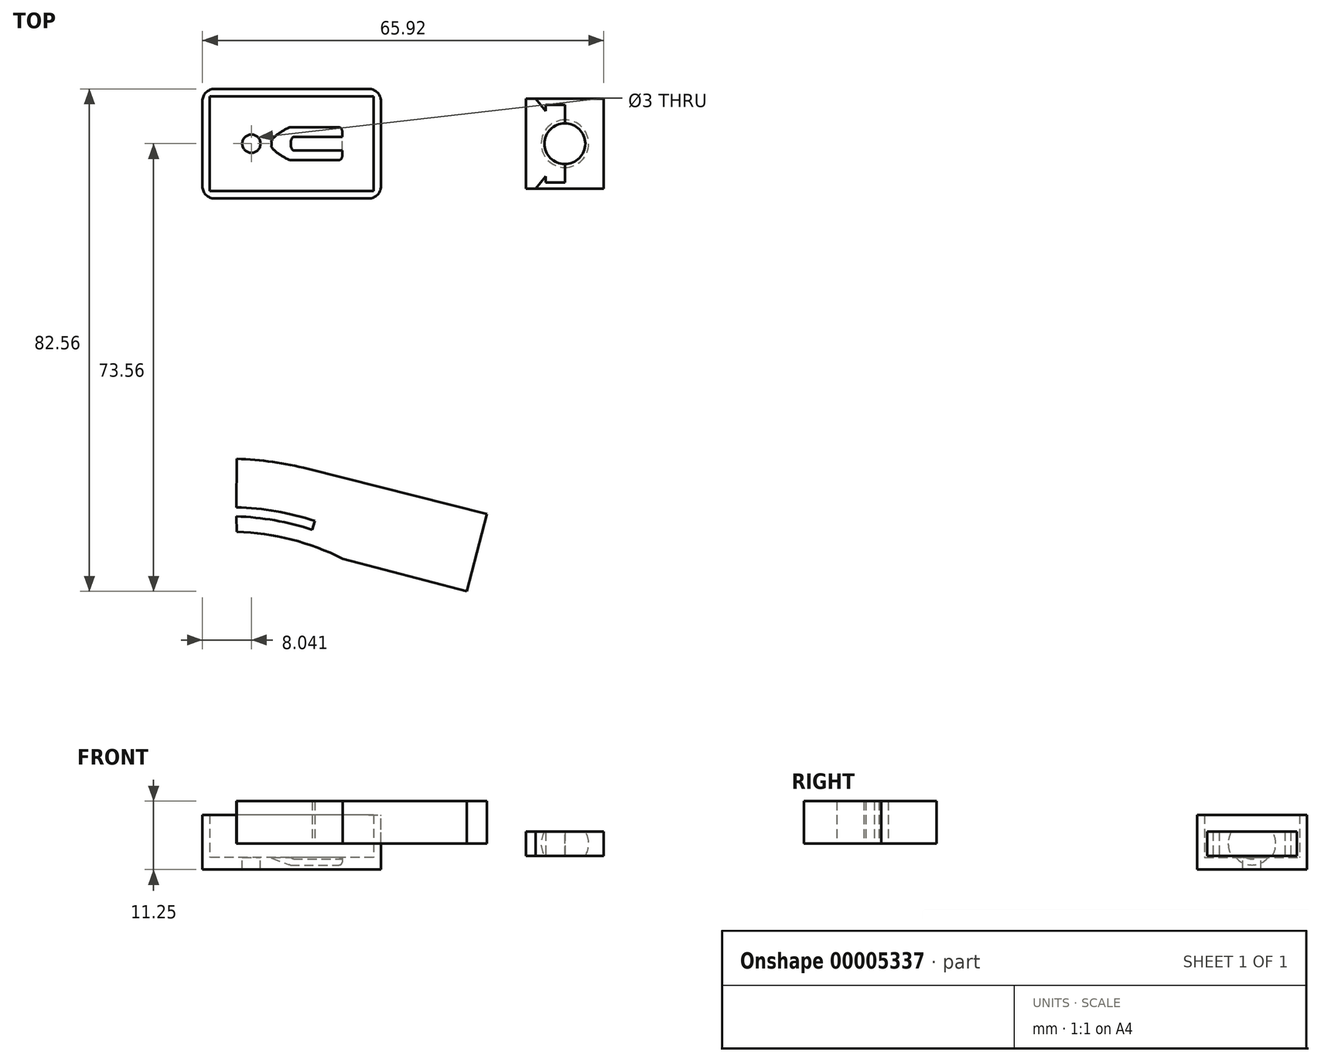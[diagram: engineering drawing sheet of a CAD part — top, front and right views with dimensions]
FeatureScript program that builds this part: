
annotation { "Feature Type Name" : "Feature", "Feature Type Description" : "" }
export const myFeature = defineFeature(function(context is Context, id is Id, definition is map)
    precondition{}
    {
        {
            var Q0;
            Q0=qCreatedBy(makeId("Top.planeOp"),FACE);
            var sketch = newSketch(context, id + "F0", { "sketchPlane" : qUnion([Q0])});
            skLineSegment(sketch, "E0", {"start": v(-22.32, 3.5) * mm, "end": v(-14.3, 3.5) * mm});
            skLineSegment(sketch, "E1", {"start": v(-13.8, 3) * mm, "end": v(-13.8, 2.5) * mm});
            skLineSegment(sketch, "E2", {"start": v(-13.8, 2.5) * mm, "end": v(-21.8, 2.5) * mm});
            skLineSegment(sketch, "E3", {"start": v(-22.3, 2) * mm, "end": v(-22.3, 0) * mm});
            skPoint(sketch, "E4.orphan", {"position": v(-13.8, 0) * mm});
            skLineSegment(sketch, "E5", {"start": v(-34.86, 0) * mm, "end": v(-13.8, 0) * mm});
            skPoint(sketch, "E6.visualSharp", {"position": v(-22.62, 3.5) * mm});
            skArc(sketch, "E6.filletArc", {"start": v(-22.32, 3.5) * mm, "mid": v(-22.51, 3.48) * mm, "end": v(-22.7, 3.43) * mm});
            skPoint(sketch, "E7.visualSharp", {"position": v(-22.3, 2.5) * mm});
            skArc(sketch, "E7.filletArc", {"start": v(-21.8, 2.5) * mm, "mid": v(-22.16, 2.35) * mm, "end": v(-22.3, 2) * mm});
            skPoint(sketch, "E8.visualSharp", {"position": v(-13.8, 3.5) * mm});
            skArc(sketch, "E8.filletArc", {"start": v(-13.8, 3) * mm, "mid": v(-13.95, 3.35) * mm, "end": v(-14.3, 3.5) * mm});
            skCircle(sketch, "E9", {"center": v(-28.72, 0) * mm, "radius": 4 * mm});
            skLineSegment(sketch, "E10", {"start": v(-22.7, 3.43) * mm, "end": v(-25.45, 2.3) * mm});
            skSolve(sketch);
        }
        {
            var Q0;
            Q0=makeQuery(id+"F0.imprint","IMPRINT",FACE,{"disambiguationData":[TD([[makeQuery(id+"F0.imprint","IMPRINT",EDGE,{"derivedFrom":sQuery(id+"F0.wireOp",EDGE,"E0")}),-1.0]])]});
            var Q1;
            Q1=sQuery(id+"F0.wireOp",EDGE,"E5");
            revolve(context, id + "F1", {"entities" : qUnion([Q0]), "axis" : qUnion([Q1]), "revolveType" : RevolveType.FULL});
        }
        {
            var Q0;
            Q0=makeQuery(id+"F1.opRevolve","SWEPT_FACE",FACE,{"disambiguationData":[OSD([sQuery(id+"F0.wireOp",EDGE,"E1")])]});
            var sketch = newSketch(context, id + "F2", { "sketchPlane" : qUnion([Q0])});
            skLineSegment(sketch, "E11.bottom", {"start": v(5.18, -2.25) * mm, "end": v(-5.15, -2.25) * mm});
            skLineSegment(sketch, "E11.top", {"start": v(5.18, 2.25) * mm, "end": v(-5.15, 2.25) * mm});
            skLineSegment(sketch, "E11.left", {"start": v(5.18, -2.25) * mm, "end": v(5.18, 2.25) * mm});
            skLineSegment(sketch, "E11.right", {"start": v(-5.15, -2.25) * mm, "end": v(-5.15, 2.25) * mm});
            skSolve(sketch);
        }
        {
            var Q0;
            Q0 = qSketchRegion(id + "F2", true);
            extrude(context, id + "F3", {"entities" : qUnion([Q0]), "operationType" : NewBodyOperationType.INTERSECT, "oppositeDirection" : true, "depth" : 30 * mm});
        }
        {
            var Q0;
            Q0=makeQuery(id+"F3.boolean.opBoolean","COPY",FACE,{"disambiguationData":[OD(0.0)],"derivedFrom":makeQuery(id+"F3.opExtrude","SWEPT_FACE",FACE,{"disambiguationData":[OSD([sQuery(id+"F2.wireOp",EDGE,"E11.top")])]})});
            var sketch = newSketch(context, id + "F4", { "sketchPlane" : qUnion([Q0])});
            skCircle(sketch, "E12.0", {"center": v(-28.72, 0) * mm, "radius": 4 * mm});
            skCircle(sketch, "E13", {"center": v(-28.72, 0) * mm, "radius": 1.5 * mm});
            skSolve(sketch);
        }
        {
            var Q0;
            Q0=makeQuery(id+"F3.boolean.opBoolean","COPY",FACE,{"derivedFrom":makeQuery(id+"F3.opExtrude","SWEPT_FACE",FACE,{"disambiguationData":[OSD([sQuery(id+"F2.wireOp",EDGE,"E11.bottom")])]})});
            var sketch = newSketch(context, id + "F5", { "sketchPlane" : qUnion([Q0])});
            skLineSegment(sketch, "E14.bottom", {"start": v(-7.44, 9) * mm, "end": v(-36.76, 9) * mm});
            skLineSegment(sketch, "E14.top", {"start": v(-7.44, -9) * mm, "end": v(-36.76, -9) * mm});
            skLineSegment(sketch, "E14.left", {"start": v(-7.44, 9) * mm, "end": v(-7.44, -9) * mm});
            skLineSegment(sketch, "E14.right", {"start": v(-36.76, 9) * mm, "end": v(-36.76, -9) * mm});
            skSolve(sketch);
        }
        {
            var Q0;
            Q0=makeQuery(id+"F5.imprint","IMPRINT",FACE,{"disambiguationData":[TD([[makeQuery(id+"F5.imprint","IMPRINT",EDGE,{"derivedFrom":sQuery(id+"F5.wireOp",EDGE,"E14.bottom")}),1.0]])]});
            var Q1;
            {var subQ0=sQuery(id+"F2.wireOp",EDGE,"E11.bottom");var subQ1=makeQuery(id+"F3.opExtrude","CAP_EDGE",EDGE,{"disambiguationData":[OSD([subQ0])],"isStart":true});Q1=makeQuery(id+"F5.imprint","IMPRINT",FACE,{"disambiguationData":[TD([[makeQuery(id+"F5.imprint","IMPRINT",EDGE,{"derivedFrom":makeQuery(id+"F3.boolean.opBoolean","COPY",EDGE,{"disambiguationData":[OD(0.0)],"derivedFrom":subQ1})}),1.0]])]});}
            extrude(context, id + "F6", {"entities" : qUnion([Q0, Q1]), "operationType" : NewBodyOperationType.ADD, "depth" : 2 * mm});
        }
        {
            var Q0;
            Q0=makeQuery(id+"F4.imprint","IMPRINT",FACE,{"disambiguationData":[TD([[makeQuery(id+"F4.imprint","IMPRINT",EDGE,{"derivedFrom":sQuery(id+"F4.wireOp",EDGE,"E13")}),1.0]])]});
            extrude(context, id + "F7", {"entities" : qUnion([Q0]), "operationType" : NewBodyOperationType.REMOVE, "oppositeDirection" : true, "depth" : 25 * mm});
        }
        {
            var Q0;
            {var subQ0=sQuery(id+"F0.wireOp",EDGE,"E9");var subQ1=sQuery(id+"F0.wireOp",EDGE,"E5");var subQ2=makeQuery(id+"F0.imprint","INTERSECT",VERTEX,{"disambiguationData":[OD(0.0)],"derivedFrom":[subQ1,subQ0]});Q0=makeQuery(id+"F0.imprint","IMPRINT",FACE,{"disambiguationData":[TD([[makeQuery(id+"F0.imprint","IMPRINT",EDGE,{"disambiguationData":[TD([[subQ2,-1.0]])],"derivedFrom":subQ1}),1.0]])]});}
            var Q1;
            Q1=sQuery(id+"F0.wireOp",EDGE,"E5");
            revolve(context, id + "F8", {"operationType" : NewBodyOperationType.REMOVE, "entities" : qUnion([Q0]), "axis" : qUnion([Q1]), "revolveType" : RevolveType.FULL, "oppositeDirection" : true});
        }
        {
            var Q0;
            Q0=makeQuery(id+"F6.opExtrude","CAP_FACE",FACE,{"disambiguationData":[OSD([sQuery(id+"F5.wireOp",EDGE,"E14.bottom"),sQuery(id+"F5.wireOp",EDGE,"E14.top"),sQuery(id+"F5.wireOp",EDGE,"E14.left"),sQuery(id+"F5.wireOp",EDGE,"E14.right")])],"isStart":true});
            var sketch = newSketch(context, id + "F9", { "sketchPlane" : qUnion([Q0])});
            skLineSegment(sketch, "E15.0", {"start": v(-7.44, 9) * mm, "end": v(-36.76, 9) * mm});
            skLineSegment(sketch, "E16.0", {"start": v(-36.76, -9) * mm, "end": v(-36.76, 9) * mm});
            skLineSegment(sketch, "E17.0", {"start": v(-7.44, -9) * mm, "end": v(-7.44, 9) * mm});
            skLineSegment(sketch, "E18.0", {"start": v(-7.44, -9) * mm, "end": v(-36.76, -9) * mm});
            skLineSegment(sketch, "E19.0", {"start": v(-8.64, 7.8) * mm, "end": v(-35.56, 7.8) * mm});
            skLineSegment(sketch, "E19.1", {"start": v(-8.64, -7.8) * mm, "end": v(-8.64, 7.8) * mm});
            skLineSegment(sketch, "E19.2", {"start": v(-8.64, -7.8) * mm, "end": v(-35.56, -7.8) * mm});
            skLineSegment(sketch, "E19.3", {"start": v(-35.56, -7.8) * mm, "end": v(-35.56, 7.8) * mm});
            skSolve(sketch);
        }
        {
            var Q0;
            Q0=makeQuery(id+"F4.imprint","IMPRINT",FACE,{"disambiguationData":[TD([[makeQuery(id+"F4.imprint","IMPRINT",EDGE,{"derivedFrom":sQuery(id+"F4.wireOp",EDGE,"E13")}),1.0]])]});
            extrude(context, id + "F10", {"entities" : qUnion([Q0]), "operationType" : NewBodyOperationType.REMOVE, "oppositeDirection" : true, "depth" : 25 * mm});
        }
        {
            var Q0;
            Q0=makeQuery(id+"F9.imprint","IMPRINT",FACE,{"disambiguationData":[TD([[makeQuery(id+"F9.imprint","IMPRINT",EDGE,{"derivedFrom":sQuery(id+"F9.wireOp",EDGE,"E15.0")}),1.0]])]});
            extrude(context, id + "F11", {"entities" : qUnion([Q0]), "operationType" : NewBodyOperationType.ADD, "depth" : 7 * mm});
        }
        {
            var Q0;
            {var subQ1=sQuery(id+"F2.wireOp",EDGE,"E11.top");var subQ6=makeQuery(id+"F3.opExtrude","CAP_EDGE",EDGE,{"disambiguationData":[OSD([subQ1])],"isStart":true});Q0=makeQuery(id+"F4.imprint","IMPRINT",FACE,{"disambiguationData":[TD([[makeQuery(id+"F4.imprint","IMPRINT",EDGE,{"derivedFrom":makeQuery(id+"F3.boolean.opBoolean","COPY",EDGE,{"disambiguationData":[OD(0.0)],"derivedFrom":subQ6})}),-1.0]])]});}
            var sketch = newSketch(context, id + "F12", { "sketchPlane" : qUnion([Q0])});
            skLineSegment(sketch, "E20.bottom", {"start": v(-22.1, 1.75) * mm, "end": v(-11.6, 1.75) * mm});
            skLineSegment(sketch, "E20.top", {"start": v(-22.1, -1.75) * mm, "end": v(-11.6, -1.75) * mm});
            skLineSegment(sketch, "E20.left", {"start": v(-22.1, 1.75) * mm, "end": v(-22.1, -1.75) * mm});
            skLineSegment(sketch, "E20.right", {"start": v(-11.6, 1.75) * mm, "end": v(-11.6, -1.75) * mm});
            skLineSegment(sketch, "E21", {"start": v(-11.6, 0) * mm, "end": v(-18.36, 0) * mm, "construction": true});
            skSolve(sketch);
        }
        {
            var Q0;
            Q0 = qSketchRegion(id + "F12", true);
            extrude(context, id + "F13", {"entities" : qUnion([Q0]), "operationType" : NewBodyOperationType.REMOVE, "oppositeDirection" : true, "depth" : 4.5 * mm});
        }
        {
            var Q0;
            Q0=makeQuery(id+"F11.boolean.opBoolean","MERGE",EDGE,{"derivedFrom":[makeQuery(id+"F6.opExtrude","SWEPT_EDGE",EDGE,{"disambiguationData":[OSD([sQuery(id+"F5.wireOp",EDGE,"E14.bottom"),sQuery(id+"F5.wireOp",EDGE,"E14.right")])]}),makeQuery(id+"F11.opExtrude","SWEPT_EDGE",EDGE,{"disambiguationData":[OSD([sQuery(id+"F9.wireOp",EDGE,"E16.0"),sQuery(id+"F9.wireOp",EDGE,"E18.0")])]})]});
            var Q1;
            Q1=makeQuery(id+"F11.boolean.opBoolean","MERGE",EDGE,{"derivedFrom":[makeQuery(id+"F6.opExtrude","SWEPT_EDGE",EDGE,{"disambiguationData":[OSD([sQuery(id+"F5.wireOp",EDGE,"E14.bottom"),sQuery(id+"F5.wireOp",EDGE,"E14.left")])]}),makeQuery(id+"F11.opExtrude","SWEPT_EDGE",EDGE,{"disambiguationData":[OSD([sQuery(id+"F9.wireOp",EDGE,"E17.0"),sQuery(id+"F9.wireOp",EDGE,"E18.0")])]})]});
            var Q2;
            Q2=makeQuery(id+"F11.boolean.opBoolean","MERGE",EDGE,{"derivedFrom":[makeQuery(id+"F6.opExtrude","SWEPT_EDGE",EDGE,{"disambiguationData":[OSD([sQuery(id+"F5.wireOp",EDGE,"E14.top"),sQuery(id+"F5.wireOp",EDGE,"E14.left")])]}),makeQuery(id+"F11.opExtrude","SWEPT_EDGE",EDGE,{"disambiguationData":[OSD([sQuery(id+"F9.wireOp",EDGE,"E15.0"),sQuery(id+"F9.wireOp",EDGE,"E17.0")])]})]});
            var Q3;
            Q3=makeQuery(id+"F11.boolean.opBoolean","MERGE",EDGE,{"derivedFrom":[makeQuery(id+"F6.opExtrude","SWEPT_EDGE",EDGE,{"disambiguationData":[OSD([sQuery(id+"F5.wireOp",EDGE,"E14.top"),sQuery(id+"F5.wireOp",EDGE,"E14.right")])]}),makeQuery(id+"F11.opExtrude","SWEPT_EDGE",EDGE,{"disambiguationData":[OSD([sQuery(id+"F9.wireOp",EDGE,"E15.0"),sQuery(id+"F9.wireOp",EDGE,"E16.0")])]})]});
            fillet(context, id + "F14", {"entities" : qUnion([Q0, Q1, Q2, Q3]), "radius" : 2 * mm, "tangentPropagation" : true, "allowEdgeOverflow" : false});
        }
        {
            var Q0;
            Q0=qCreatedBy(makeId("Top.planeOp"),FACE);
            var sketch = newSketch(context, id + "F15", { "sketchPlane" : qUnion([Q0])});
            skLineSegment(sketch, "E22.bottom", {"start": v(16.4, 7.39) * mm, "end": v(29.16, 7.39) * mm});
            skLineSegment(sketch, "E22.top", {"start": v(16.4, -7.39) * mm, "end": v(29.16, -7.39) * mm});
            skLineSegment(sketch, "E22.left", {"start": v(16.4, 7.39) * mm, "end": v(16.4, -7.39) * mm});
            skLineSegment(sketch, "E22.right", {"start": v(29.16, 7.39) * mm, "end": v(29.16, -7.39) * mm});
            skLineSegment(sketch, "E23", {"start": v(22.78, 7.39) * mm, "end": v(22.78, -7.39) * mm});
            skArc(sketch, "E24", {"start": v(22.78, -3.9) * mm, "mid": v(26.68, 0) * mm, "end": v(22.78, 3.9) * mm});
            skLineSegment(sketch, "E25", {"start": v(22.78, 6.39) * mm, "end": v(19.64, 6.39) * mm});
            skLineSegment(sketch, "E26", {"start": v(19.64, 6.39) * mm, "end": v(19.64, 5.39) * mm});
            skLineSegment(sketch, "E27", {"start": v(19.64, 5.39) * mm, "end": v(17.96, 7.39) * mm});
            skLineSegment(sketch, "E28.0.MirrorCS", {"start": v(19.64, -5.39) * mm, "end": v(17.96, -7.39) * mm});
            skLineSegment(sketch, "E29.0.MirrorCS", {"start": v(19.64, -6.39) * mm, "end": v(19.64, -5.39) * mm});
            skLineSegment(sketch, "E30.0.MirrorCS", {"start": v(22.78, -6.39) * mm, "end": v(19.64, -6.39) * mm});
            skSolve(sketch);
        }
        {
            var Q0;
            {var subQ8=sQuery(id+"F15.wireOp",EDGE,"E22.left");Q0=makeQuery(id+"F15.imprint","IMPRINT",FACE,{"disambiguationData":[TD([[makeQuery(id+"F15.imprint","IMPRINT",EDGE,{"derivedFrom":subQ8}),1.0]])]});}
            var Q1;
            {var subQ0=sQuery(id+"F15.wireOp",EDGE,"E24");var subQ1=sQuery(id+"F15.wireOp",EDGE,"E23");var subQ3=makeQuery(id+"F15.imprint","INTERSECT",VERTEX,{"disambiguationData":[OD(0.0)],"derivedFrom":[subQ1,subQ0]});Q1=makeQuery(id+"F15.imprint","IMPRINT",FACE,{"disambiguationData":[TD([[makeQuery(id+"F15.imprint","IMPRINT",EDGE,{"disambiguationData":[TD([[subQ3,-1.0]])],"derivedFrom":subQ1}),-1.0]])]});}
            extrude(context, id + "F16", {"entities" : qUnion([Q0, Q1]), "endBound" : BoundingType.SYMMETRIC, "depth" : 4 * mm});
        }
        {
            var Q0;
            {var subQ1=sQuery(id+"F15.wireOp",EDGE,"E25");Q0=makeQuery(id+"F15.imprint","IMPRINT",FACE,{"disambiguationData":[TD([[makeQuery(id+"F15.imprint","IMPRINT",EDGE,{"derivedFrom":subQ1}),-1.0]])]});}
            var Q1;
            {var subQ10=sQuery(id+"F15.wireOp",EDGE,"E22.right");Q1=makeQuery(id+"F15.imprint","IMPRINT",FACE,{"disambiguationData":[TD([[makeQuery(id+"F15.imprint","IMPRINT",EDGE,{"derivedFrom":subQ10}),-1.0]])]});}
            var Q2;
            {var subQ0=sQuery(id+"F15.wireOp",EDGE,"E24");var subQ1=sQuery(id+"F15.wireOp",EDGE,"E23");var subQ3=makeQuery(id+"F15.imprint","INTERSECT",VERTEX,{"disambiguationData":[OD(0.0)],"derivedFrom":[subQ1,subQ0]});Q2=makeQuery(id+"F15.imprint","IMPRINT",FACE,{"disambiguationData":[TD([[makeQuery(id+"F15.imprint","IMPRINT",EDGE,{"disambiguationData":[TD([[subQ3,-1.0]])],"derivedFrom":subQ1}),1.0]])]});}
            var Q3;
            {var subQ1=sQuery(id+"F15.wireOp",EDGE,"E28.0.MirrorCS");Q3=makeQuery(id+"F15.imprint","IMPRINT",FACE,{"disambiguationData":[TD([[makeQuery(id+"F15.imprint","IMPRINT",EDGE,{"derivedFrom":subQ1}),1.0]])]});}
            var Q4;
            {var subQ0=sQuery(id+"F15.wireOp",EDGE,"E24");Q4=makeQuery(id+"F15.imprint","IMPRINT",FACE,{"disambiguationData":[TD([[makeQuery(id+"F15.imprint","IMPRINT",EDGE,{"derivedFrom":subQ0}),1.0]])]});}
            extrude(context, id + "F17", {"entities" : qUnion([Q0, Q1, Q2, Q3, Q4]), "endBound" : BoundingType.SYMMETRIC, "depth" : 4 * mm});
        }
        {
            var Q0;
            {var subQ0=sQuery(id+"F15.wireOp",EDGE,"E24");Q0=makeQuery(id+"F15.imprint","IMPRINT",FACE,{"disambiguationData":[TD([[makeQuery(id+"F15.imprint","IMPRINT",EDGE,{"derivedFrom":subQ0}),1.0]])]});}
            var Q1;
            Q1=sQuery(id+"F15.wireOp",EDGE,"E23");
            revolve(context, id + "F18", {"operationType" : NewBodyOperationType.REMOVE, "entities" : qUnion([Q0]), "axis" : qUnion([Q1]), "revolveType" : RevolveType.FULL, "oppositeDirection" : true});
        }
        {
            var Q0;
            Q0=qCreatedBy(makeId("Top.planeOp"),FACE);
            var sketch = newSketch(context, id + "F19", { "sketchPlane" : qUnion([Q0])});
            skArc(sketch, "E31.0", {"start": v(0, -62.7) * mm, "mid": v(-14.72, -54.86) * mm, "end": v(-31.1, -51.8) * mm});
            skArc(sketch, "E32.trimOffspring", {"start": v(-13.74, -68.22) * mm, "mid": v(-22.18, -65.05) * mm, "end": v(-31.1, -63.77) * mm});
            skArc(sketch, "E33.0", {"start": v(-18.74, -63.45) * mm, "mid": v(-24.9, -61.9) * mm, "end": v(-31.2, -61.27) * mm});
            skArc(sketch, "E34.0", {"start": v(-18.31, -62) * mm, "mid": v(-24.66, -60.43) * mm, "end": v(-31.17, -59.77) * mm});
            skLineSegment(sketch, "E35", {"start": v(-18.74, -63.45) * mm, "end": v(-18.31, -62) * mm});
            skLineSegment(sketch, "E36", {"start": v(-2.13, -71.26) * mm, "end": v(0, -62.7) * mm});
            skLineSegment(sketch, "E37", {"start": v(-18.74, -66.09) * mm, "end": v(-13.66, -55.24) * mm});
            skLineSegment(sketch, "E38", {"start": v(-31.2, -61.27) * mm, "end": v(-31.1, -63.77) * mm});
            skLineSegment(sketch, "E39", {"start": v(-31.17, -59.77) * mm, "end": v(-31.1, -51.8) * mm});
            skLineSegment(sketch, "E40", {"start": v(-13.74, -68.22) * mm, "end": v(6.64, -73.56) * mm});
            skLineSegment(sketch, "E41", {"start": v(6.64, -73.56) * mm, "end": v(9.97, -60.86) * mm});
            skLineSegment(sketch, "E42", {"start": v(9.97, -60.86) * mm, "end": v(-19.46, -53.43) * mm});
            skSolve(sketch);
        }
        {
            var Q0;
            Q0=makeQuery(id+"F19.imprint","IMPRINT",FACE,{"disambiguationData":[TD([[makeQuery(id+"F19.imprint","IMPRINT",EDGE,{"derivedFrom":sQuery(id+"F19.wireOp",EDGE,"E33.0")}),1.0]])]});
            var Q1;
            {var subQ1=sQuery(id+"F19.wireOp",EDGE,"E36");Q1=makeQuery(id+"F19.imprint","IMPRINT",FACE,{"disambiguationData":[TD([[makeQuery(id+"F19.imprint","IMPRINT",EDGE,{"derivedFrom":subQ1}),1.0]])]});}
            var Q2;
            {var subQ3=sQuery(id+"F19.wireOp",EDGE,"E36");Q2=makeQuery(id+"F19.imprint","IMPRINT",FACE,{"disambiguationData":[TD([[makeQuery(id+"F19.imprint","IMPRINT",EDGE,{"derivedFrom":subQ3}),-1.0]])]});}
            extrude(context, id + "F20", {"entities" : qUnion([Q0, Q1, Q2]), "depth" : 7 * mm});
        }
    });
